# Revit family: Valve-Four_Outlet_Thermostatic-KOHLER-Anthem-K-26342BR_1
name_source: partatom
category: Plumbing Fixtures
units: mm (PartAtom-declared; Revit-internal decimal feet)

## family parameters
Cut with Voids When Loaded = No
Host = Face
Maintain Annotation Orientation = No
OmniClass Number = 23.27.31.00
OmniClass Title = Valves
Part Type = Normal
Room Calculation Point = No
Round Connector Dimension = Use Diameter
Shared = No

## types (1)
- NA-Not Applicable
    ADA Compliant = No
    Assembly Code = D2020
    CW Connection = Yes
    Cold Water Inlet = Cold Water Inlet
    Date Modified = 05/09/2022
    Default Elevation = 42"
    Description = 4-OUTLET VALVE PUSH BUTTON THERMOSTATIC VALVE
    Finish = Kohler-Plastic-58-Thunder_Grey
    Flow Rate = 11 GPM
    HW Connection = Yes
    Height = 4 7/8"
    Hot Water Inlet = Hot Water Inlet
    Length = 6 1/8"
    Manufacturer = Kohler Co.
    Master Format 2014 = 23 09 13.33
    Master Format 2014 Name = Control Valves
    Material = Brass Construction
    Model = K-26342BR-NA
    Pressure = 60.00 psi
    Product Name = Anthem
    Tempered Water Outlet 1 = Tempered Water Outlet 1
    Tempered Water Outlet 2 = Tempered Water Outlet 2
    Tempered Water Outlet 3 = Tempered Water Outlet 3
    Tempered Water Outlet 4 = Tempered Water Outlet 4
    Type = 1
    URL = https://br.kohler.com
    Vent Connection = No
    Waste Connection = No
    WaterSense Certified = No
    Width = 16 1/2"

## geometry (parser evidence)
native form markers: Sweep x6
no freeform markers — native parametric forms only
